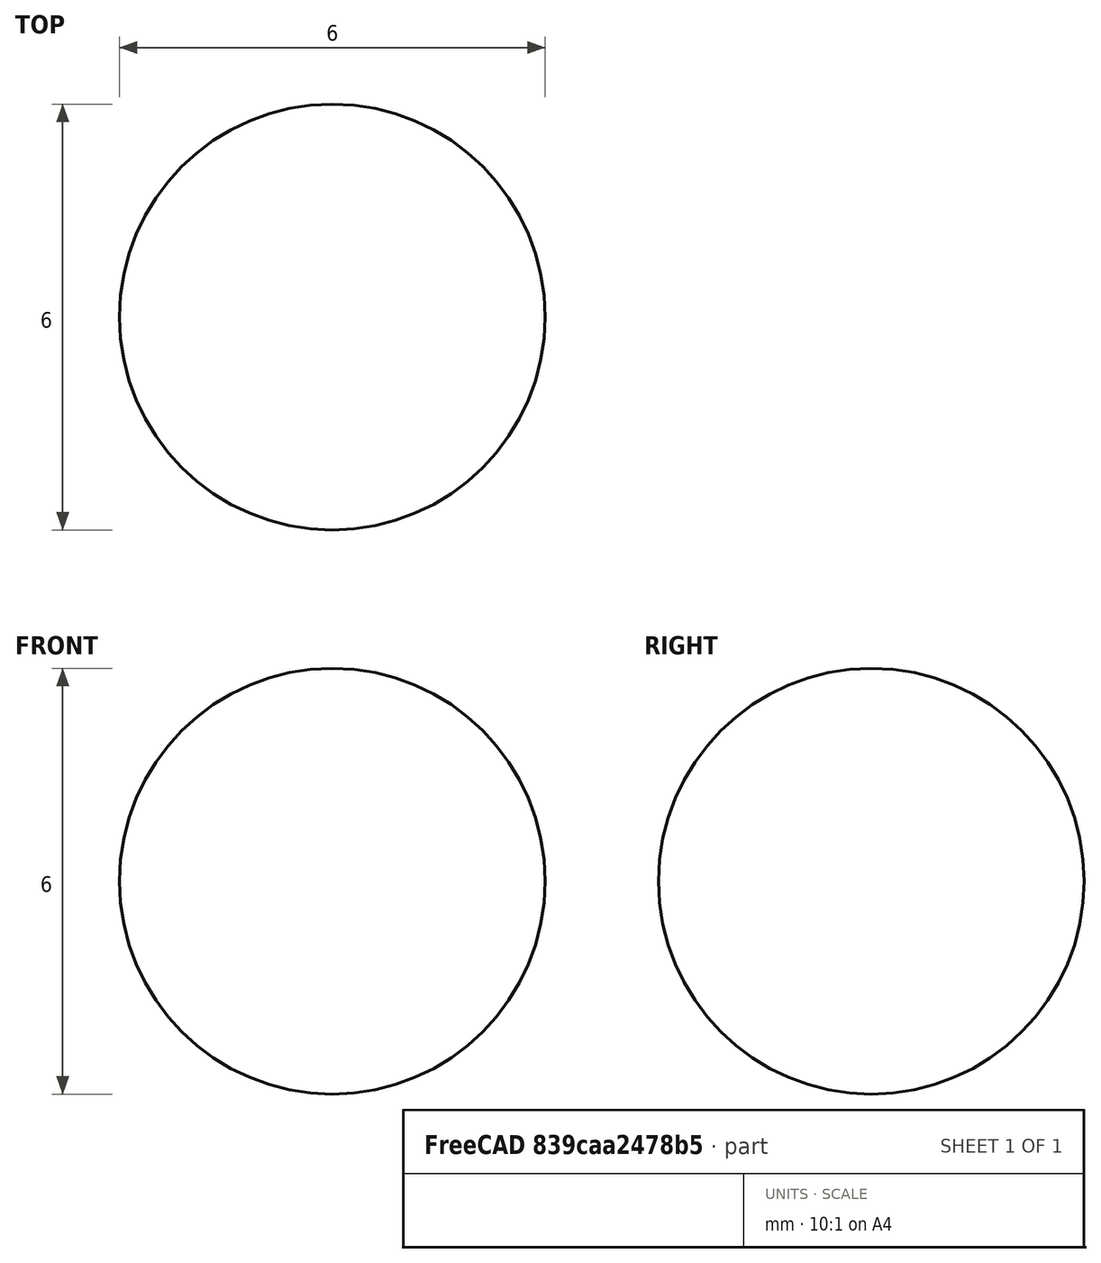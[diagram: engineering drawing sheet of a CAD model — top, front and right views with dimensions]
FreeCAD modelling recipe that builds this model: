
FCSTD DOCUMENT  (FreeCAD 0.19R24212 (Git))
Label: ball
License: All rights reserved
LicenseURL: http://en.wikipedia.org/wiki/All_rights_reserved
objects: Sketcher::SketchObject×1, PartDesign::Revolution×1, PartDesign::Body×1
note: 4 computed .brp shape members not serialized (recipe doc carries the construction recipe); baked Part::Feature solids carry a one-line shape summary decoded from their .brp

FEATURE [Sketcher::SketchObject] Sketch
  FullyConstrained = true
  MapMode = 5
  Support = -> [XY_Plane]
  sketch-geometry (2):
    g0: ArcOfCircle CenterX=0 CenterY=0 CenterZ=0 NormalX=0 NormalY=0 NormalZ=1 AngleXU=0 Radius=3 StartAngle=1.5708 EndAngle=4.71239
    g1: LineSegment StartX=0 StartY=-3 StartZ=0 EndX=2e-16 EndY=3 EndZ=0
  constraints (6):
    c: Coincident(g0,g-1)
    c: PointOnObject(g0,g-2)
    c: PointOnObject(g0,g-2)
    c: Coincident(g1,g0)
    c: Coincident(g1,g0)
    c: Radius(g0) = 3
FEATURE [PartDesign::Revolution] Revolution
  Angle = 360
  Axis = (0,1,0)
  Base = (0,0,0)
  Profile = -> Sketch
  ReferenceAxis = -> Sketch [V_Axis]
FEATURE [PartDesign::Body] Body
  Group = -> [Sketch,Revolution]
  Origin = -> Origin
  Tip = -> Revolution
